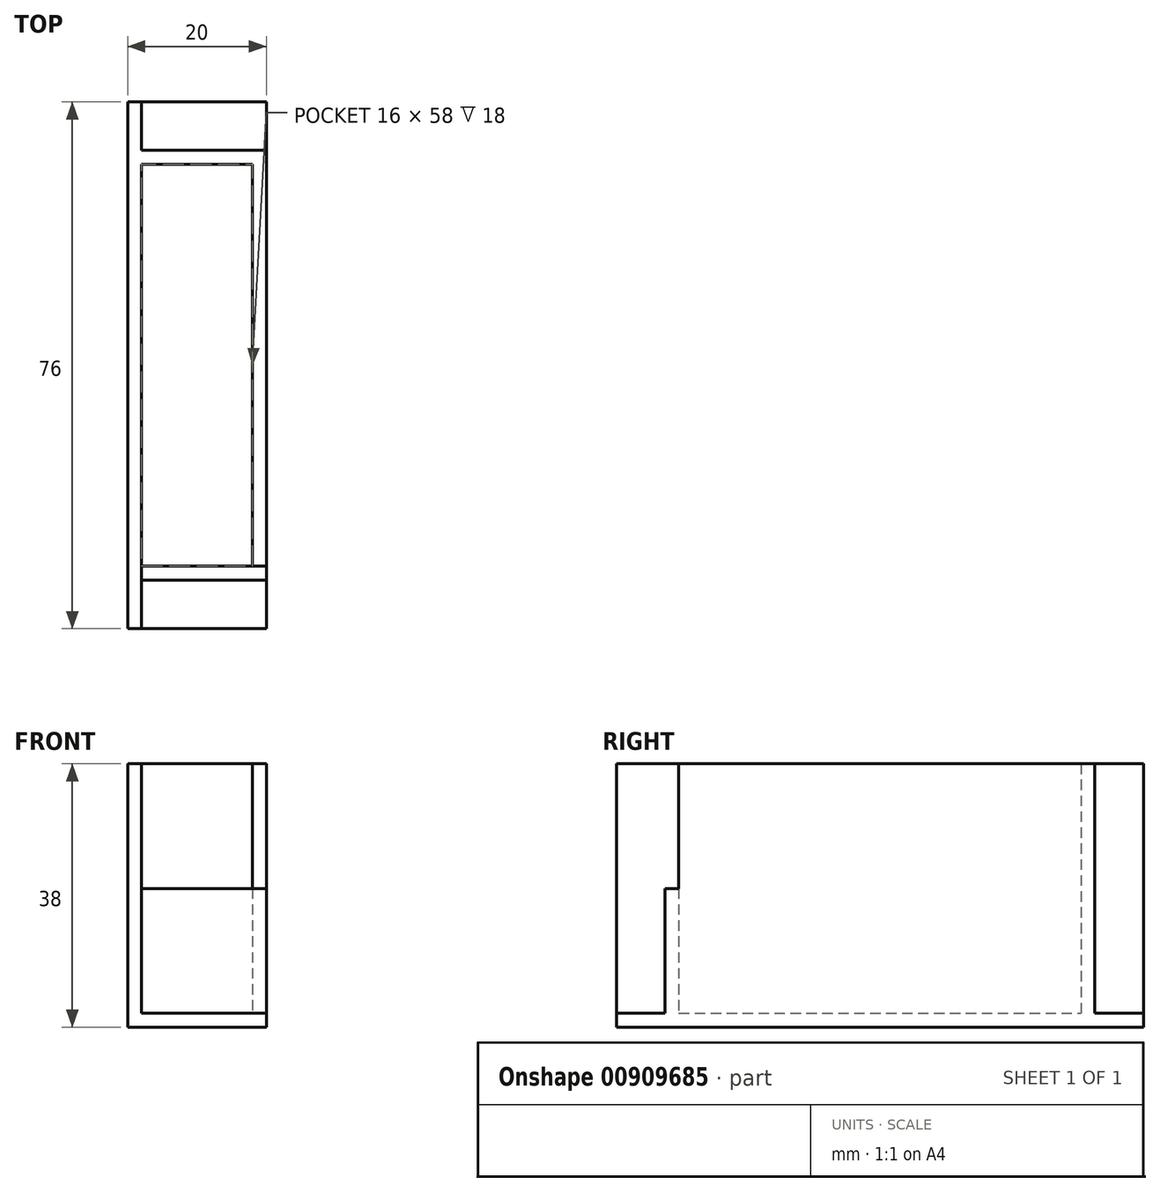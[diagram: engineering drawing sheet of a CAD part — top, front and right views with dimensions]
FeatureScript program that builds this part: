
annotation { "Feature Type Name" : "Feature", "Feature Type Description" : "" }
export const myFeature = defineFeature(function(context is Context, id is Id, definition is map)
    precondition{}
    {
        {
            var Q0;
            Q0=qCreatedBy(makeId("Top.planeOp"),FACE);
            var sketch = newSketch(context, id + "F0", { "sketchPlane" : qUnion([Q0])});
            skLineSegment(sketch, "E0.bottom", {"start": v(0, 0) * mm, "end": v(16, 0) * mm});
            skLineSegment(sketch, "E0.top", {"start": v(0, 58) * mm, "end": v(16, 58) * mm});
            skLineSegment(sketch, "E0.left", {"start": v(0, 0) * mm, "end": v(0, 58) * mm});
            skLineSegment(sketch, "E0.right", {"start": v(16, 0) * mm, "end": v(16, 58) * mm});
            skLineSegment(sketch, "E1.0", {"start": v(-2, -2) * mm, "end": v(-2, 60) * mm});
            skLineSegment(sketch, "E1.1", {"start": v(-2, -2) * mm, "end": v(18, -2) * mm});
            skLineSegment(sketch, "E1.2", {"start": v(18, -2) * mm, "end": v(18, 60) * mm});
            skLineSegment(sketch, "E1.3", {"start": v(-2, 60) * mm, "end": v(18, 60) * mm});
            skLineSegment(sketch, "E2.0", {"start": v(-2, 67) * mm, "end": v(18, 67) * mm});
            skLineSegment(sketch, "E3.0", {"start": v(-2, -9) * mm, "end": v(18, -9) * mm});
            skLineSegment(sketch, "E4", {"start": v(-2, 67) * mm, "end": v(-2, 60) * mm});
            skLineSegment(sketch, "E5", {"start": v(18, 67) * mm, "end": v(18, 60) * mm});
            skLineSegment(sketch, "E6", {"start": v(-2, -9) * mm, "end": v(-2, -2) * mm});
            skLineSegment(sketch, "E7", {"start": v(18, -9) * mm, "end": v(18, -2) * mm});
            skLineSegment(sketch, "E8.left", {"start": v(-2, 67) * mm, "end": v(-2, -9) * mm});
            skLineSegment(sketch, "E8.right", {"start": v(18, 67) * mm, "end": v(18, -9) * mm});
            skSolve(sketch);
        }
        {
            var Q0;
            Q0=makeQuery(id+"F0.imprint","IMPRINT",FACE,{"disambiguationData":[TD([[makeQuery(id+"F0.imprint","IMPRINT",EDGE,{"derivedFrom":sQuery(id+"F0.wireOp",EDGE,"E1.3")}),1.0]])]});
            var Q1;
            Q1=makeQuery(id+"F0.imprint","IMPRINT",FACE,{"disambiguationData":[TD([[makeQuery(id+"F0.imprint","IMPRINT",EDGE,{"derivedFrom":sQuery(id+"F0.wireOp",EDGE,"E0.bottom")}),-1.0]])]});
            var Q2;
            Q2=makeQuery(id+"F0.imprint","IMPRINT",FACE,{"disambiguationData":[TD([[makeQuery(id+"F0.imprint","IMPRINT",EDGE,{"derivedFrom":sQuery(id+"F0.wireOp",EDGE,"E0.bottom")}),1.0]])]});
            var Q3;
            Q3=makeQuery(id+"F0.imprint","IMPRINT",FACE,{"disambiguationData":[TD([[makeQuery(id+"F0.imprint","IMPRINT",EDGE,{"derivedFrom":sQuery(id+"F0.wireOp",EDGE,"E1.1")}),-1.0]])]});
            extrude(context, id + "F1", {"entities" : qUnion([Q0, Q1, Q2, Q3]), "oppositeDirection" : true, "depth" : 2 * mm, "offsetDistance" : 25 * mm});
        }
        {
            var Q0;
            Q0=makeQuery(id+"F0.imprint","IMPRINT",FACE,{"disambiguationData":[TD([[makeQuery(id+"F0.imprint","IMPRINT",EDGE,{"derivedFrom":sQuery(id+"F0.wireOp",EDGE,"E0.bottom")}),-1.0]])]});
            extrude(context, id + "F2", {"entities" : qUnion([Q0]), "operationType" : NewBodyOperationType.ADD, "depth" : 36 * mm, "offsetDistance" : 25 * mm});
        }
        {
            var Q0;
            Q0=makeQuery(id+"F2.opExtrude","SWEPT_FACE",FACE,{"disambiguationData":[OSD([sQuery(id+"F0.wireOp",EDGE,"E1.1")])]});
            var sketch = newSketch(context, id + "F3", { "sketchPlane" : qUnion([Q0])});
            skLineSegment(sketch, "E9.bottom", {"start": v(-2, 36) * mm, "end": v(0, 36) * mm});
            skLineSegment(sketch, "E9.top", {"start": v(-2, 0) * mm, "end": v(0, 0) * mm});
            skLineSegment(sketch, "E9.left", {"start": v(-2, 36) * mm, "end": v(-2, 0) * mm});
            skLineSegment(sketch, "E9.right", {"start": v(0, 36) * mm, "end": v(0, 0) * mm});
            skSolve(sketch);
        }
        {
            var Q0;
            Q0 = qSketchRegion(id + "F3", true);
            extrude(context, id + "F4", {"entities" : qUnion([Q0]), "operationType" : NewBodyOperationType.ADD, "depth" : 7 * mm, "offsetDistance" : 25 * mm});
        }
        {
            var Q0;
            Q0=makeQuery(id+"F2.opExtrude","SWEPT_FACE",FACE,{"disambiguationData":[OSD([sQuery(id+"F0.wireOp",EDGE,"E1.3")])]});
            var sketch = newSketch(context, id + "F5", { "sketchPlane" : qUnion([Q0])});
            skLineSegment(sketch, "E10.bottom", {"start": v(2, 36) * mm, "end": v(0, 36) * mm});
            skLineSegment(sketch, "E10.top", {"start": v(2, 0) * mm, "end": v(0, 0) * mm});
            skLineSegment(sketch, "E10.left", {"start": v(2, 36) * mm, "end": v(2, 0) * mm});
            skLineSegment(sketch, "E10.right", {"start": v(0, 36) * mm, "end": v(0, 0) * mm});
            skSolve(sketch);
        }
        {
            var Q0;
            Q0 = qSketchRegion(id + "F5", true);
            extrude(context, id + "F6", {"entities" : qUnion([Q0]), "operationType" : NewBodyOperationType.ADD, "depth" : 7 * mm, "offsetDistance" : 25 * mm});
        }
        {
            var Q0;
            Q0=makeQuery(id+"F6.boolean.opBoolean","MERGE",FACE,{"derivedFrom":[makeQuery(id+"F4.boolean.opBoolean","MERGE",FACE,{"derivedFrom":[makeQuery(id+"F2.opExtrude","CAP_FACE",FACE,{"disambiguationData":[OSD([sQuery(id+"F0.wireOp",EDGE,"E0.bottom"),sQuery(id+"F0.wireOp",EDGE,"E0.top"),sQuery(id+"F0.wireOp",EDGE,"E0.left"),sQuery(id+"F0.wireOp",EDGE,"E0.right"),sQuery(id+"F0.wireOp",EDGE,"E1.0"),sQuery(id+"F0.wireOp",EDGE,"E1.1"),sQuery(id+"F0.wireOp",EDGE,"E1.2"),sQuery(id+"F0.wireOp",EDGE,"E1.3")])],"isStart":false}),makeQuery(id+"F4.opExtrude","SWEPT_FACE",FACE,{"disambiguationData":[OSD([sQuery(id+"F3.wireOp",EDGE,"E9.bottom")])]})]}),makeQuery(id+"F6.opExtrude","SWEPT_FACE",FACE,{"disambiguationData":[OSD([sQuery(id+"F5.wireOp",EDGE,"E10.bottom")])]})]});
            var sketch = newSketch(context, id + "F7", { "sketchPlane" : qUnion([Q0])});
            skLineSegment(sketch, "E11.bottom", {"start": v(18, -2) * mm, "end": v(0, -2) * mm});
            skLineSegment(sketch, "E11.top", {"start": v(18, 0) * mm, "end": v(0, 0) * mm});
            skLineSegment(sketch, "E11.left", {"start": v(18, -2) * mm, "end": v(18, 0) * mm});
            skLineSegment(sketch, "E11.right", {"start": v(0, -2) * mm, "end": v(0, 0) * mm});
            skSolve(sketch);
        }
        {
            var Q0;
            Q0 = qSketchRegion(id + "F7", true);
            extrude(context, id + "F8", {"entities" : qUnion([Q0]), "operationType" : NewBodyOperationType.REMOVE, "oppositeDirection" : true, "depth" : 18 * mm, "offsetDistance" : 25 * mm});
        }
    });
